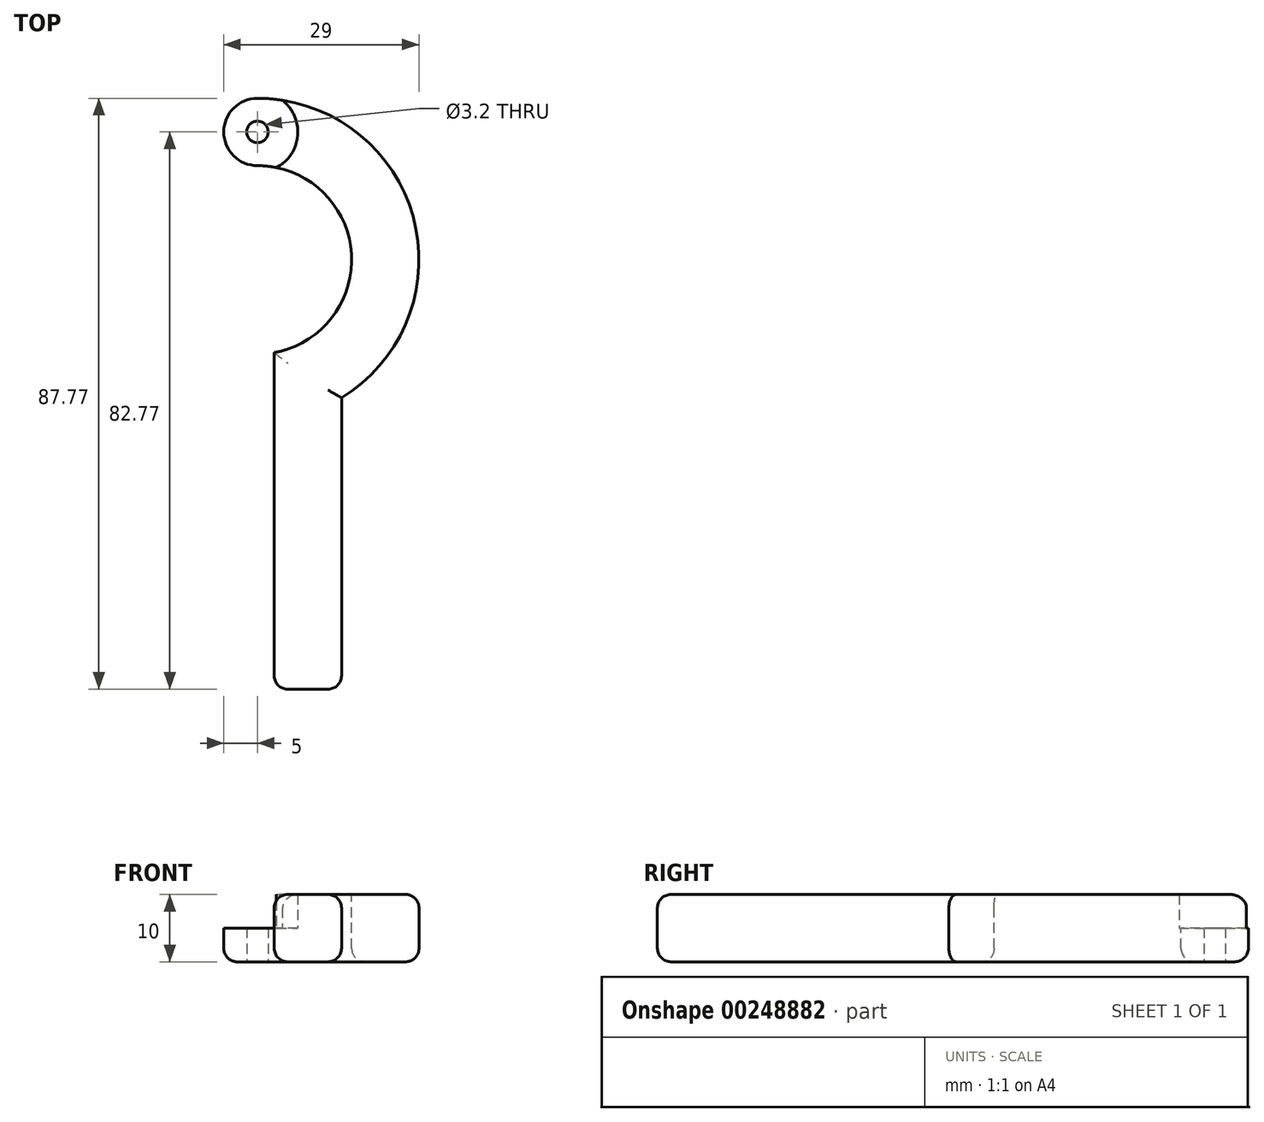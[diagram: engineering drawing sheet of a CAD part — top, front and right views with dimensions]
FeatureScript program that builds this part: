
annotation { "Feature Type Name" : "Feature", "Feature Type Description" : "" }
export const myFeature = defineFeature(function(context is Context, id is Id, definition is map)
    precondition{}
    {
        {
            var Q0;
            Q0=qCreatedBy(makeId("Top.planeOp"),FACE);
            var sketch = newSketch(context, id + "F0", { "sketchPlane" : qUnion([Q0])});
            skArc(sketch, "E0", {"start": v(2.5, -13.77) * mm, "mid": v(13.94, 1.26) * mm, "end": v(0, 14) * mm});
            skLineSegment(sketch, "E1", {"start": v(0, -14) * mm, "end": v(0, 0) * mm, "construction": true});
            skLineSegment(sketch, "E2", {"start": v(-2.5, 0) * mm, "end": v(2.5, 0) * mm, "construction": true});
            skLineSegment(sketch, "E3", {"start": v(2.5, -13.77) * mm, "end": v(2.5, -63.77) * mm});
            skLineSegment(sketch, "E4", {"start": v(2.5, 0) * mm, "end": v(2.5, -13.77) * mm, "construction": true});
            skLineSegment(sketch, "E5", {"start": v(0, 0) * mm, "end": v(0, 14) * mm, "construction": true});
            skSolve(sketch);
        }
        {
            var Q0;
            Q0=qCreatedBy(makeId("Front.planeOp"),FACE);
            var Q1;
            Q1=sQuery(id+"F0.wireOp",VERTEX,"E3.end");
            cPlane(context, id + "F1", {"entities" : qUnion([Q0, Q1]), "cplaneType" : CPlaneType.PLANE_POINT, "offset" : 25 * mm, "width" : 150 * mm, "height" : 150 * mm});
        }
        {
            var Q0;
            Q0=qCreatedBy(id+"F1.planeOp",FACE);
            var sketch = newSketch(context, id + "F2", { "sketchPlane" : qUnion([Q0])});
            skLineSegment(sketch, "E6.bottom", {"start": v(2.5, 0) * mm, "end": v(12.5, 0) * mm});
            skLineSegment(sketch, "E6.top", {"start": v(2.5, 10) * mm, "end": v(12.5, 10) * mm});
            skLineSegment(sketch, "E6.left", {"start": v(2.5, 0) * mm, "end": v(2.5, 10) * mm});
            skLineSegment(sketch, "E6.right", {"start": v(12.5, 0) * mm, "end": v(12.5, 10) * mm});
            skSolve(sketch);
        }
        {
            var Q0;
            Q0 = qSketchRegion(id + "F2", true);
            var Q1;
            Q1 = qConstructionFilter(qBodyType(qCreatedBy(id + "F0" ,EDGE), BodyType.WIRE), ConstructionObject.NO);
            sweep(context, id + "F3", {"profiles" : qUnion([Q0]), "path" : qUnion([Q1])});
        }
        {
            var Q0;
            Q0=qCreatedBy(makeId("Top.planeOp"),FACE);
            var sketch = newSketch(context, id + "F4", { "sketchPlane" : qUnion([Q0])});
            skCircle(sketch, "E7", {"center": v(0, 19) * mm, "radius": 5 * mm});
            skSolve(sketch);
        }
        {
            var Q0;
            Q0 = qSketchRegion(id + "F4", true);
            extrude(context, id + "F5", {"entities" : qUnion([Q0]), "operationType" : NewBodyOperationType.ADD, "depth" : 5 * mm});
        }
        {
            var Q0;
            Q0=makeQuery(id+"F5.opExtrude","CAP_FACE",FACE,{"disambiguationData":[OSD([sQuery(id+"F4.wireOp",EDGE,"E7")])],"isStart":false});
            var sketch = newSketch(context, id + "F6", { "sketchPlane" : qUnion([Q0])});
            skCircle(sketch, "E8", {"center": v(0, 19) * mm, "radius": 6 * mm});
            skSolve(sketch);
        }
        {
            var Q0;
            Q0 = qSketchRegion(id + "F6", true);
            extrude(context, id + "F7", {"entities" : qUnion([Q0]), "operationType" : NewBodyOperationType.REMOVE, "endBound" : BoundingType.THROUGH_ALL, "depth" : 25 * mm});
        }
        {
            var Q0;
            Q0=qCreatedBy(makeId("Top.planeOp"),FACE);
            var sketch = newSketch(context, id + "F8", { "sketchPlane" : qUnion([Q0])});
            skCircle(sketch, "E9", {"center": v(0, 19) * mm, "radius": 1.6 * mm});
            skSolve(sketch);
        }
        {
            var Q0;
            Q0 = qSketchRegion(id + "F8", true);
            extrude(context, id + "F9", {"entities" : qUnion([Q0]), "operationType" : NewBodyOperationType.REMOVE, "endBound" : BoundingType.THROUGH_ALL, "depth" : 25 * mm});
        }
        {
            var Q0;
            Q0=makeQuery(id+"F3.opSweep","SWEPT_EDGE",EDGE,{"disambiguationData":[OSD([sQuery(id+"F0.wireOp",EDGE,"E3"),sQuery(id+"F2.wireOp",EDGE,"E6.top"),sQuery(id+"F2.wireOp",EDGE,"E6.left")])]});
            var Q1;
            Q1=makeQuery(id+"F3.opSweep","SWEPT_EDGE",EDGE,{"disambiguationData":[OSD([sQuery(id+"F0.wireOp",EDGE,"E3"),sQuery(id+"F2.wireOp",EDGE,"E6.bottom"),sQuery(id+"F2.wireOp",EDGE,"E6.left")])]});
            var Q2;
            Q2=makeQuery(id+"F3.opSweep","CAP_EDGE",EDGE,{"disambiguationData":[OSD([sQuery(id+"F0.wireOp",VERTEX,"E3.end"),sQuery(id+"F2.wireOp",EDGE,"E6.left")])],"isStart":true});
            var Q3;
            Q3=makeQuery(id+"F3.opSweep","CAP_EDGE",EDGE,{"disambiguationData":[OSD([sQuery(id+"F0.wireOp",VERTEX,"E3.end"),sQuery(id+"F2.wireOp",EDGE,"E6.right")])],"isStart":true});
            var Q4;
            Q4=makeQuery(id+"F3.opSweep","SWEPT_EDGE",EDGE,{"disambiguationData":[OSD([sQuery(id+"F0.wireOp",EDGE,"E3"),sQuery(id+"F2.wireOp",EDGE,"E6.top"),sQuery(id+"F2.wireOp",EDGE,"E6.right")])]});
            var Q5;
            Q5=makeQuery(id+"F3.opSweep","SWEPT_EDGE",EDGE,{"disambiguationData":[OSD([sQuery(id+"F0.wireOp",EDGE,"E0"),sQuery(id+"F2.wireOp",EDGE,"E6.top"),sQuery(id+"F2.wireOp",EDGE,"E6.right")])]});
            var Q6;
            Q6=makeQuery(id+"F3.opSweep","SWEPT_EDGE",EDGE,{"disambiguationData":[OSD([sQuery(id+"F0.wireOp",EDGE,"E3"),sQuery(id+"F2.wireOp",EDGE,"E6.bottom"),sQuery(id+"F2.wireOp",EDGE,"E6.right")])]});
            var Q7;
            Q7=makeQuery(id+"F3.opSweep","CAP_FACE",FACE,{"disambiguationData":[OSD([sQuery(id+"F0.wireOp",VERTEX,"E3.end"),sQuery(id+"F2.wireOp",EDGE,"E6.bottom"),sQuery(id+"F2.wireOp",EDGE,"E6.top"),sQuery(id+"F2.wireOp",EDGE,"E6.left"),sQuery(id+"F2.wireOp",EDGE,"E6.right")])],"isStart":true});
            var Q8;
            Q8=makeQuery(id+"F3.opSweep","SWEPT_EDGE",EDGE,{"disambiguationData":[OSD([sQuery(id+"F0.wireOp",EDGE,"E0"),sQuery(id+"F2.wireOp",EDGE,"E6.bottom"),sQuery(id+"F2.wireOp",EDGE,"E6.right")])]});
            fillet(context, id + "F10", {"entities" : qUnion([Q0, Q1, Q2, Q3, Q4, Q5, Q6, Q7, Q8]), "radius" : 2 * mm, "tangentPropagation" : true, "allowEdgeOverflow" : false});
        }
    });
